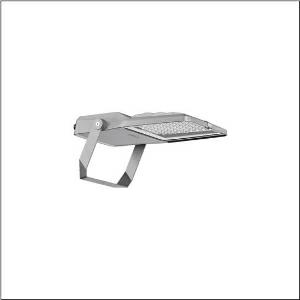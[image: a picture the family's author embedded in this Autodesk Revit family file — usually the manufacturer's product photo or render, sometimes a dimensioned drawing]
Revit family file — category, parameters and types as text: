
# Revit family: floodlight_fl_21_iq_mini___pl33t_5xa7772d4f1a_39e2
name_source: partatom
category: Lighting Fixtures
units: mm (PartAtom-declared; Revit-internal decimal feet)

## family parameters
Cut with Voids When Loaded = No
Host = Face
Light Source = No
Part Type = Normal
Room Calculation Point = No
Round Connector Dimension = Use Diameter
Shared = No

## types (1)
- --- (1 x LED, 18390 lm, 143 W, 4000K)
    Apparent Load = 143 VA
    CIE Flux Codes = 26 75 99 100 100
    Color Rendering = 70
    Color Temperature = 4000K
    Default Elevation = 1800 mm
    Description = Floodlight FL 21 iQ mini, floodlight, primary light control with lens, of PMMA, primary optical cover: protective disc, of toughened safety glass, transparent, light distribution: PL33T, light emission: direct distribution, installation type: surface-mounted, lamps: LED, High Power LED, rated values: 18.390lm | 143W | 128,6lm/W (begin service life); end service life: 18.390lm | 151,6W; at 50% lumin. flux: 9.195lm | 60,8W | 151,2lm/W, colour temperature: 4000K, colour rendering: CRI > 70, light colour: 740, light setting 1 begin service life: 100% | 18.390lm | 143W | 128,6lm/W | 4.000K, light setting 1 end service life: 151,6W, further light settings possible, control: Street-Remote, Auto-Match, Temp-Guard, Night-Set, Smart-Wire, Desk-Remote (wireless, voltage-free reading and setting of iQ features in the workshop via application-optimized NFC function/RFID function), optimised constant luminous flux control (CLO 2.0), pre-setting: linear dimming characteristic, with terminal, 6-pole, mains connection: 220..240V, AC, 50/60Hz, luminaire housing, of diecast aluminium, powder-coated, SITECO metallic grey (DB 702S), corrosivity category C5 mid according to DIN EN ISO 12944suitable for swimming poolschlorine-resistant, sealing non-destructively replaceable, mounting bracket, of steel, galvanised, powder-coated, SITECO metallic grey (DB 702S), protection rating (complete): IP66, insulation class (complete): insulation class II (safety insulation), certification: CE, ENEC, VDE, protection symbol: D, impact resistance: IK08, permissible operating ambient temperature: -40..+40°C, permissible operating ambient temperature for outdoor applications: -40..+50°C, standard: DIN EN 12944, LABS conformity tested according to VDMA 24364:2018-05, packaging unit: 1 piece

Light Distribution: PL33T
    Height = 70 mm
    Lamp = 1 x LED
    Lamp Light Flux = 18390 lm
    Lamp Power = 143 W
    Lamp count = 1
    Length = 485 mm
    Luminous efficacy = 129 lm/W
    Manufacturer = Siteco
    ModVariant = No
    Model = 5XA7772D4F1A
    Number of Poles = 1
    OnlyDefault = Yes
    Power Factor = 1
    Product Name = Floodlight FL 21 iQ mini | PL33T
    Product group = floodlight | pylon annexe
    ProductGroupID = 6201
    Protection Class = Protection class II
    Protection Degree = IP 66
    RLX_Detail_Level = 1
    RLX_Emergency_Light_Flux = 0 lm
    RLX_Emergency_Type = 0
    RLX_Emergency_Type_DB = No
    RlxData = <blob elided: 96549 chars, md5=66860be3>
    Socket = socket
    Standby Power = 0 W
    System Light Flux = 18390 lm
    System Power = 143 W
    Type Comments = factory setting: luminous flux: 100 % | dim-lin: 254 | 730 mA
    Type Image = l_1006845.jpg
    URL = http://relux.com
    VarID = @adj_148351
    Voltage = 0 V
    Weight = 0.00 kg
    Width = 337 mm

## geometry (parser evidence)
native form markers: Blend x4, Sweep x11
no freeform markers — native parametric forms only
